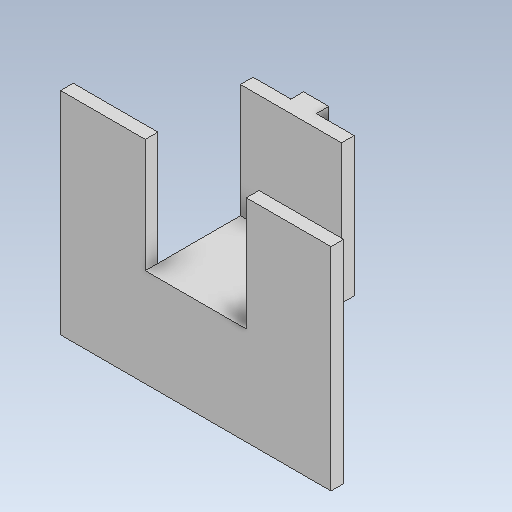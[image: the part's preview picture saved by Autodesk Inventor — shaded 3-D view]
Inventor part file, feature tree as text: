
AUTODESK INVENTOR PART (.ipt)
format: ipt  version: 2020 (Build 240168000, 168)  size: 161,792 bytes
history: native  units: mm
features: reference x20, other x12, extrude x4, sketch x4, projected_geometry x3
ambient origin geometry x8: Origin, YZ Plane, XZ Plane, XY Plane, X Axis, Y Axis, Z Axis, Center Point
bodies: Body1 (feature_tree)
feature tree (43):
  other  "솔리드1"
  extrude  "돌출1"  Depth=10.0mm TaperAngle=0.0deg
  sketch  "스케치2"
  other  "작업 평면1"
  extrude  "돌출2"  Depth=90.0mm
  extrude  "돌출3"  Depth=10.0mm TaperAngle=0.0deg
  extrude  "돌출4"  Depth=10.0mm TaperAngle=0.0deg
  sketch  "스케치1"
  reference  "참조1"
  reference  "참조2"
  reference  "참조3"
  reference  "참조4"
  reference  "참조5"
  reference  "참조6"
  reference  "참조7"
  reference  "참조8"
  reference  "참조9"
  reference  "참조10"
  reference  "참조11"
  projected_geometry  "투영된 루프1"
  sketch  "스케치3"
  projected_geometry  "투영된 루프2"
  reference  "참조13"
  reference  "참조14"
  reference  "참조15"
  reference  "참조16"
  sketch  "스케치4"
  reference  "참조17"
  reference  "참조18"
  reference  "참조19"
  reference  "참조20"
  reference  "참조21"
  projected_geometry  "투영된 루프3"
  other  "<userpath>\Documents\Inventor\CoMoVi\Package\v6.iam"
  other  "v6.iam"
  other  "AL_profile_final:2"
  other  "AL_profile_final:1"
  other  "caster_wheel_mount:1"
  other  "tray4_L:1"
  other  "tray4_R:1"
  other  "cross_AL_profile:1"
  other  "horiz_bar:1"
  other  "cross_AL_profile:2"
